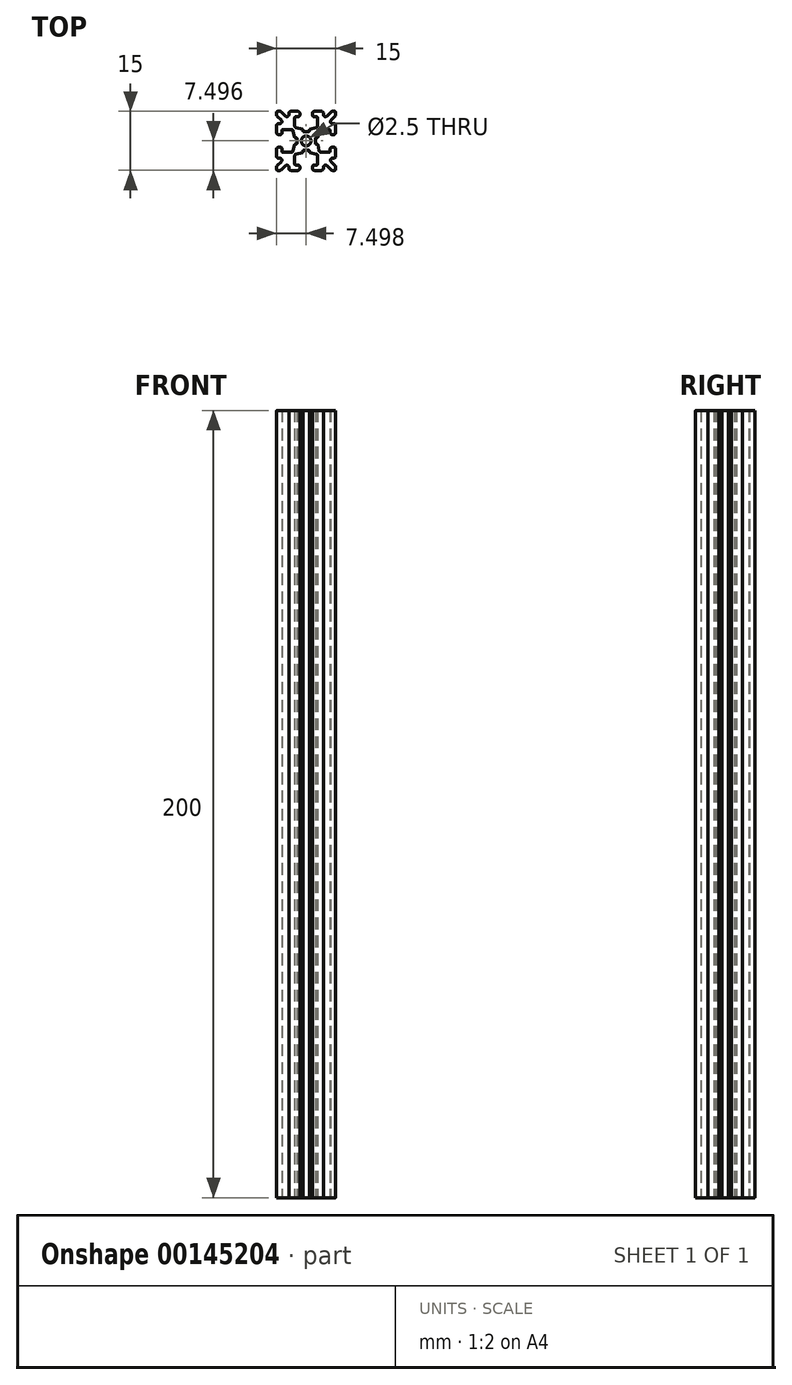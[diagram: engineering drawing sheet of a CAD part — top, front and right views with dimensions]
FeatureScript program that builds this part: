
annotation { "Feature Type Name" : "Feature", "Feature Type Description" : "" }
export const myFeature = defineFeature(function(context is Context, id is Id, definition is map)
    precondition{}
    {
        {
            var Q0;
            Q0=qCreatedBy(makeId("Top.planeOp"),FACE);
            var sketch = newSketch(context, id + "F0", { "sketchPlane" : qUnion([Q0])});
            skCircle(sketch, "E0", {"center": v(-4.16, 17.74) * mm, "radius": 1.25 * mm});
            skArc(sketch, "E1", {"start": v(-3.34, 15.19) * mm, "mid": v(-3.4, 15.33) * mm, "end": v(-3.54, 15.39) * mm});
            skLineSegment(sketch, "E2", {"start": v(-3.54, 15.39) * mm, "end": v(-4.79, 15.39) * mm});
            skArc(sketch, "E3", {"start": v(-4.79, 15.39) * mm, "mid": v(-4.93, 15.33) * mm, "end": v(-4.99, 15.19) * mm});
            skLineSegment(sketch, "E4", {"start": v(-4.99, 15.19) * mm, "end": v(-4.99, 14.96) * mm});
            skArc(sketch, "E5", {"start": v(-5.14, 14.77) * mm, "mid": v(-5.03, 14.84) * mm, "end": v(-4.99, 14.96) * mm});
            skLineSegment(sketch, "E6", {"start": v(-5.14, 14.77) * mm, "end": v(-6.67, 14.42) * mm});
            skArc(sketch, "E7", {"start": v(-6.67, 14.42) * mm, "mid": v(-6.95, 14.25) * mm, "end": v(-7.06, 13.94) * mm});
            skLineSegment(sketch, "E8", {"start": v(-7.06, 13.94) * mm, "end": v(-7.06, 11.84) * mm});
            skArc(sketch, "E9", {"start": v(-7.06, 11.84) * mm, "mid": v(-7, 11.7) * mm, "end": v(-6.86, 11.64) * mm});
            skLineSegment(sketch, "E10", {"start": v(-6.86, 11.64) * mm, "end": v(-6.26, 11.64) * mm});
            skArc(sketch, "E11", {"start": v(-5.76, 11.14) * mm, "mid": v(-5.9, 11.49) * mm, "end": v(-6.26, 11.64) * mm});
            skLineSegment(sketch, "E12", {"start": v(-5.76, 11.14) * mm, "end": v(-5.76, 10.74) * mm});
            skArc(sketch, "E13", {"start": v(-6.26, 10.24) * mm, "mid": v(-5.9, 10.38) * mm, "end": v(-5.76, 10.74) * mm});
            skArc(sketch, "E14", {"start": v(-8.56, 10.74) * mm, "mid": v(-8.42, 10.38) * mm, "end": v(-8.06, 10.24) * mm});
            skLineSegment(sketch, "E15", {"start": v(-8.56, 10.74) * mm, "end": v(-8.56, 11.07) * mm});
            skArc(sketch, "E16", {"start": v(-8.56, 11.07) * mm, "mid": v(-8.87, 11.53) * mm, "end": v(-9.42, 11.42) * mm});
            skLineSegment(sketch, "E17", {"start": v(-9.42, 11.42) * mm, "end": v(-10.45, 10.38) * mm});
            skArc(sketch, "E18", {"start": v(-10.8, 10.24) * mm, "mid": v(-10.62, 10.27) * mm, "end": v(-10.45, 10.38) * mm});
            skArc(sketch, "E19", {"start": v(-11.66, 10.49) * mm, "mid": v(-11.59, 10.3) * mm, "end": v(-11.41, 10.24) * mm});
            skArc(sketch, "E20", {"start": v(-11.52, 11.44) * mm, "mid": v(-11.62, 11.28) * mm, "end": v(-11.66, 11.09) * mm});
            skLineSegment(sketch, "E21", {"start": v(-11.52, 11.44) * mm, "end": v(-10.48, 12.48) * mm});
            skArc(sketch, "E22", {"start": v(-10.48, 12.48) * mm, "mid": v(-10.37, 13.03) * mm, "end": v(-10.83, 13.34) * mm});
            skLineSegment(sketch, "E23", {"start": v(-10.83, 13.34) * mm, "end": v(-11.16, 13.34) * mm});
            skArc(sketch, "E24", {"start": v(-11.66, 13.84) * mm, "mid": v(-11.52, 13.48) * mm, "end": v(-11.16, 13.34) * mm});
            skLineSegment(sketch, "E25", {"start": v(-11.66, 15.64) * mm, "end": v(-11.66, 13.84) * mm});
            skArc(sketch, "E26", {"start": v(-11.16, 16.14) * mm, "mid": v(-11.52, 15.99) * mm, "end": v(-11.66, 15.64) * mm});
            skLineSegment(sketch, "E27", {"start": v(-11.16, 16.14) * mm, "end": v(-10.76, 16.14) * mm});
            skArc(sketch, "E28", {"start": v(-10.26, 15.64) * mm, "mid": v(-10.4, 15.99) * mm, "end": v(-10.76, 16.14) * mm});
            skLineSegment(sketch, "E29", {"start": v(-10.26, 15.64) * mm, "end": v(-10.26, 15.04) * mm});
            skArc(sketch, "E30", {"start": v(-10.26, 15.04) * mm, "mid": v(-10.2, 14.9) * mm, "end": v(-10.06, 14.84) * mm});
            skLineSegment(sketch, "E31", {"start": v(-10.06, 14.84) * mm, "end": v(-7.96, 14.84) * mm});
            skArc(sketch, "E32", {"start": v(-7.96, 14.84) * mm, "mid": v(-7.65, 14.95) * mm, "end": v(-7.47, 15.23) * mm});
            skLineSegment(sketch, "E33", {"start": v(-7.47, 15.23) * mm, "end": v(-7.13, 16.75) * mm});
            skArc(sketch, "E34", {"start": v(-6.94, 16.91) * mm, "mid": v(-7.06, 16.87) * mm, "end": v(-7.13, 16.75) * mm});
            skLineSegment(sketch, "E35", {"start": v(-6.94, 16.91) * mm, "end": v(-6.7, 16.91) * mm});
            skArc(sketch, "E36", {"start": v(-6.7, 16.91) * mm, "mid": v(-6.57, 16.97) * mm, "end": v(-6.5, 17.11) * mm});
            skLineSegment(sketch, "E37", {"start": v(-6.5, 17.11) * mm, "end": v(-6.5, 18.36) * mm});
            skArc(sketch, "E38", {"start": v(-6.5, 18.36) * mm, "mid": v(-6.57, 18.5) * mm, "end": v(-6.7, 18.56) * mm});
            skLineSegment(sketch, "E39", {"start": v(-6.7, 18.56) * mm, "end": v(-6.94, 18.56) * mm});
            skArc(sketch, "E40", {"start": v(-7.13, 18.72) * mm, "mid": v(-7.06, 18.6) * mm, "end": v(-6.94, 18.56) * mm});
            skLineSegment(sketch, "E41", {"start": v(-7.13, 18.72) * mm, "end": v(-7.47, 20.25) * mm});
            skArc(sketch, "E42", {"start": v(-7.47, 20.25) * mm, "mid": v(-7.65, 20.53) * mm, "end": v(-7.96, 20.64) * mm});
            skLineSegment(sketch, "E43", {"start": v(-7.96, 20.64) * mm, "end": v(-10.06, 20.64) * mm});
            skArc(sketch, "E44", {"start": v(-10.06, 20.64) * mm, "mid": v(-10.2, 20.58) * mm, "end": v(-10.26, 20.44) * mm});
            skLineSegment(sketch, "E45", {"start": v(-10.26, 20.44) * mm, "end": v(-10.26, 19.84) * mm});
            skArc(sketch, "E46", {"start": v(-10.76, 19.34) * mm, "mid": v(-10.4, 19.48) * mm, "end": v(-10.26, 19.84) * mm});
            skLineSegment(sketch, "E47", {"start": v(-10.76, 19.34) * mm, "end": v(-11.16, 19.34) * mm});
            skArc(sketch, "E48", {"start": v(-11.66, 19.84) * mm, "mid": v(-11.52, 19.48) * mm, "end": v(-11.16, 19.34) * mm});
            skArc(sketch, "E49", {"start": v(-11.16, 22.14) * mm, "mid": v(-11.52, 21.99) * mm, "end": v(-11.66, 21.64) * mm});
            skLineSegment(sketch, "E50", {"start": v(-11.16, 22.14) * mm, "end": v(-10.83, 22.14) * mm});
            skArc(sketch, "E51", {"start": v(-10.83, 22.14) * mm, "mid": v(-10.37, 22.44) * mm, "end": v(-10.48, 22.99) * mm});
            skLineSegment(sketch, "E52", {"start": v(-10.48, 22.99) * mm, "end": v(-11.52, 24.03) * mm});
            skArc(sketch, "E53", {"start": v(-11.66, 24.38) * mm, "mid": v(-11.62, 24.2) * mm, "end": v(-11.52, 24.03) * mm});
            skArc(sketch, "E54", {"start": v(-11.41, 25.24) * mm, "mid": v(-11.59, 25.16) * mm, "end": v(-11.66, 24.99) * mm});
            skArc(sketch, "E55", {"start": v(-10.45, 25.09) * mm, "mid": v(-10.62, 25.2) * mm, "end": v(-10.8, 25.24) * mm});
            skLineSegment(sketch, "E56", {"start": v(-10.45, 25.09) * mm, "end": v(-9.42, 24.05) * mm});
            skArc(sketch, "E57", {"start": v(-9.42, 24.05) * mm, "mid": v(-8.87, 23.94) * mm, "end": v(-8.56, 24.4) * mm});
            skLineSegment(sketch, "E58", {"start": v(-8.56, 24.4) * mm, "end": v(-8.56, 24.74) * mm});
            skArc(sketch, "E59", {"start": v(-8.06, 25.24) * mm, "mid": v(-8.42, 25.09) * mm, "end": v(-8.56, 24.74) * mm});
            skArc(sketch, "E60", {"start": v(-5.76, 24.74) * mm, "mid": v(-5.9, 25.09) * mm, "end": v(-6.26, 25.24) * mm});
            skLineSegment(sketch, "E61", {"start": v(-5.76, 24.74) * mm, "end": v(-5.76, 24.34) * mm});
            skArc(sketch, "E62", {"start": v(-6.26, 23.84) * mm, "mid": v(-5.9, 23.98) * mm, "end": v(-5.76, 24.34) * mm});
            skLineSegment(sketch, "E63", {"start": v(-6.26, 23.84) * mm, "end": v(-6.86, 23.84) * mm});
            skArc(sketch, "E64", {"start": v(-6.86, 23.84) * mm, "mid": v(-7, 23.78) * mm, "end": v(-7.06, 23.64) * mm});
            skLineSegment(sketch, "E65", {"start": v(-7.06, 23.64) * mm, "end": v(-7.06, 21.54) * mm});
            skArc(sketch, "E66", {"start": v(-7.06, 21.54) * mm, "mid": v(-6.95, 21.22) * mm, "end": v(-6.67, 21.05) * mm});
            skLineSegment(sketch, "E67", {"start": v(-6.67, 21.05) * mm, "end": v(-5.14, 20.7) * mm});
            skArc(sketch, "E68", {"start": v(-4.99, 20.51) * mm, "mid": v(-5.03, 20.64) * mm, "end": v(-5.14, 20.7) * mm});
            skLineSegment(sketch, "E69", {"start": v(-4.99, 20.51) * mm, "end": v(-4.99, 20.28) * mm});
            skArc(sketch, "E70", {"start": v(-4.99, 20.28) * mm, "mid": v(-4.93, 20.14) * mm, "end": v(-4.79, 20.08) * mm});
            skLineSegment(sketch, "E71", {"start": v(-4.79, 20.08) * mm, "end": v(-3.54, 20.08) * mm});
            skArc(sketch, "E72", {"start": v(-3.54, 20.08) * mm, "mid": v(-3.4, 20.14) * mm, "end": v(-3.34, 20.28) * mm});
            skLineSegment(sketch, "E73", {"start": v(-3.34, 20.28) * mm, "end": v(-3.34, 20.51) * mm});
            skArc(sketch, "E74", {"start": v(-3.18, 20.7) * mm, "mid": v(-3.3, 20.64) * mm, "end": v(-3.34, 20.51) * mm});
            skLineSegment(sketch, "E75", {"start": v(-3.18, 20.7) * mm, "end": v(-1.65, 21.05) * mm});
            skArc(sketch, "E76", {"start": v(-1.65, 21.05) * mm, "mid": v(-1.37, 21.22) * mm, "end": v(-1.26, 21.54) * mm});
            skLineSegment(sketch, "E77", {"start": v(-1.26, 21.54) * mm, "end": v(-1.26, 23.64) * mm});
            skArc(sketch, "E78", {"start": v(-1.26, 23.64) * mm, "mid": v(-1.32, 23.78) * mm, "end": v(-1.46, 23.84) * mm});
            skLineSegment(sketch, "E79", {"start": v(-1.46, 23.84) * mm, "end": v(-2.06, 23.84) * mm});
            skArc(sketch, "E80", {"start": v(-2.56, 24.34) * mm, "mid": v(-2.42, 23.98) * mm, "end": v(-2.06, 23.84) * mm});
            skLineSegment(sketch, "E81", {"start": v(-2.56, 24.34) * mm, "end": v(-2.56, 24.74) * mm});
            skArc(sketch, "E82", {"start": v(-2.06, 25.24) * mm, "mid": v(-2.42, 25.09) * mm, "end": v(-2.56, 24.74) * mm});
            skArc(sketch, "E83", {"start": v(0.24, 24.74) * mm, "mid": v(0.1, 25.09) * mm, "end": v(-0.26, 25.24) * mm});
            skLineSegment(sketch, "E84", {"start": v(0.24, 24.74) * mm, "end": v(0.24, 24.4) * mm});
            skArc(sketch, "E85", {"start": v(0.24, 24.4) * mm, "mid": v(0.55, 23.94) * mm, "end": v(1.1, 24.05) * mm});
            skLineSegment(sketch, "E86", {"start": v(1.1, 24.05) * mm, "end": v(2.13, 25.09) * mm});
            skArc(sketch, "E87", {"start": v(2.48, 25.24) * mm, "mid": v(2.3, 25.2) * mm, "end": v(2.13, 25.09) * mm});
            skLineSegment(sketch, "E88", {"start": v(3.09, 25.24) * mm, "end": v(2.48, 25.24) * mm});
            skArc(sketch, "E89", {"start": v(3.34, 24.99) * mm, "mid": v(3.27, 25.16) * mm, "end": v(3.09, 25.24) * mm});
            skArc(sketch, "E90", {"start": v(3.2, 24.03) * mm, "mid": v(3.3, 24.2) * mm, "end": v(3.34, 24.38) * mm});
            skLineSegment(sketch, "E91", {"start": v(3.2, 24.03) * mm, "end": v(2.15, 22.99) * mm});
            skArc(sketch, "E92", {"start": v(2.15, 22.99) * mm, "mid": v(2.04, 22.44) * mm, "end": v(2.5, 22.14) * mm});
            skLineSegment(sketch, "E93", {"start": v(2.5, 22.14) * mm, "end": v(2.84, 22.14) * mm});
            skArc(sketch, "E94", {"start": v(3.34, 21.64) * mm, "mid": v(3.2, 21.99) * mm, "end": v(2.84, 22.14) * mm});
            skArc(sketch, "E95", {"start": v(2.84, 19.34) * mm, "mid": v(3.2, 19.48) * mm, "end": v(3.34, 19.84) * mm});
            skLineSegment(sketch, "E96", {"start": v(2.84, 19.34) * mm, "end": v(2.44, 19.34) * mm});
            skArc(sketch, "E97", {"start": v(1.94, 19.84) * mm, "mid": v(2.08, 19.48) * mm, "end": v(2.44, 19.34) * mm});
            skLineSegment(sketch, "E98", {"start": v(1.94, 19.84) * mm, "end": v(1.94, 20.44) * mm});
            skArc(sketch, "E99", {"start": v(1.94, 20.44) * mm, "mid": v(1.88, 20.58) * mm, "end": v(1.74, 20.64) * mm});
            skLineSegment(sketch, "E100", {"start": v(1.74, 20.64) * mm, "end": v(-0.36, 20.64) * mm});
            skArc(sketch, "E101", {"start": v(-0.36, 20.64) * mm, "mid": v(-0.67, 20.53) * mm, "end": v(-0.85, 20.25) * mm});
            skLineSegment(sketch, "E102", {"start": v(-0.85, 20.25) * mm, "end": v(-1.2, 18.72) * mm});
            skArc(sketch, "E103", {"start": v(-1.39, 18.56) * mm, "mid": v(-1.26, 18.6) * mm, "end": v(-1.2, 18.72) * mm});
            skLineSegment(sketch, "E104", {"start": v(-1.39, 18.56) * mm, "end": v(-1.61, 18.56) * mm});
            skArc(sketch, "E105", {"start": v(-1.61, 18.56) * mm, "mid": v(-1.76, 18.5) * mm, "end": v(-1.81, 18.36) * mm});
            skLineSegment(sketch, "E106", {"start": v(-1.81, 18.36) * mm, "end": v(-1.81, 17.11) * mm});
            skArc(sketch, "E107", {"start": v(-1.81, 17.11) * mm, "mid": v(-1.76, 16.97) * mm, "end": v(-1.61, 16.91) * mm});
            skLineSegment(sketch, "E108", {"start": v(-1.61, 16.91) * mm, "end": v(-1.39, 16.91) * mm});
            skArc(sketch, "E109", {"start": v(-1.2, 16.75) * mm, "mid": v(-1.26, 16.87) * mm, "end": v(-1.39, 16.91) * mm});
            skLineSegment(sketch, "E110", {"start": v(-1.2, 16.75) * mm, "end": v(-0.85, 15.23) * mm});
            skArc(sketch, "E111", {"start": v(-0.85, 15.23) * mm, "mid": v(-0.67, 14.95) * mm, "end": v(-0.36, 14.84) * mm});
            skLineSegment(sketch, "E112", {"start": v(-0.36, 14.84) * mm, "end": v(1.74, 14.84) * mm});
            skArc(sketch, "E113", {"start": v(1.74, 14.84) * mm, "mid": v(1.88, 14.9) * mm, "end": v(1.94, 15.04) * mm});
            skLineSegment(sketch, "E114", {"start": v(1.94, 15.04) * mm, "end": v(1.94, 15.64) * mm});
            skArc(sketch, "E115", {"start": v(2.44, 16.14) * mm, "mid": v(2.08, 15.99) * mm, "end": v(1.94, 15.64) * mm});
            skLineSegment(sketch, "E116", {"start": v(2.44, 16.14) * mm, "end": v(2.84, 16.14) * mm});
            skArc(sketch, "E117", {"start": v(3.34, 15.64) * mm, "mid": v(3.2, 15.99) * mm, "end": v(2.84, 16.14) * mm});
            skLineSegment(sketch, "E118", {"start": v(3.34, 13.84) * mm, "end": v(3.34, 15.64) * mm});
            skArc(sketch, "E119", {"start": v(2.84, 13.34) * mm, "mid": v(3.2, 13.48) * mm, "end": v(3.34, 13.84) * mm});
            skLineSegment(sketch, "E120", {"start": v(2.84, 13.34) * mm, "end": v(2.5, 13.34) * mm});
            skArc(sketch, "E121", {"start": v(2.5, 13.34) * mm, "mid": v(2.04, 13.03) * mm, "end": v(2.15, 12.48) * mm});
            skLineSegment(sketch, "E122", {"start": v(2.15, 12.48) * mm, "end": v(3.2, 11.44) * mm});
            skArc(sketch, "E123", {"start": v(3.34, 11.09) * mm, "mid": v(3.3, 11.28) * mm, "end": v(3.2, 11.44) * mm});
            skArc(sketch, "E124", {"start": v(3.09, 10.24) * mm, "mid": v(3.27, 10.3) * mm, "end": v(3.34, 10.49) * mm});
            skLineSegment(sketch, "E125", {"start": v(2.48, 10.24) * mm, "end": v(3.09, 10.24) * mm});
            skArc(sketch, "E126", {"start": v(2.13, 10.38) * mm, "mid": v(2.3, 10.27) * mm, "end": v(2.48, 10.24) * mm});
            skLineSegment(sketch, "E127", {"start": v(2.13, 10.38) * mm, "end": v(1.1, 11.42) * mm});
            skArc(sketch, "E128", {"start": v(1.1, 11.42) * mm, "mid": v(0.55, 11.53) * mm, "end": v(0.24, 11.07) * mm});
            skLineSegment(sketch, "E129", {"start": v(0.24, 11.07) * mm, "end": v(0.24, 10.74) * mm});
            skArc(sketch, "E130", {"start": v(-0.26, 10.24) * mm, "mid": v(0.1, 10.38) * mm, "end": v(0.24, 10.74) * mm});
            skArc(sketch, "E131", {"start": v(-2.56, 10.74) * mm, "mid": v(-2.42, 10.38) * mm, "end": v(-2.06, 10.24) * mm});
            skLineSegment(sketch, "E132", {"start": v(-2.56, 10.74) * mm, "end": v(-2.56, 11.14) * mm});
            skArc(sketch, "E133", {"start": v(-2.06, 11.64) * mm, "mid": v(-2.42, 11.49) * mm, "end": v(-2.56, 11.14) * mm});
            skLineSegment(sketch, "E134", {"start": v(-2.06, 11.64) * mm, "end": v(-1.46, 11.64) * mm});
            skArc(sketch, "E135", {"start": v(-1.46, 11.64) * mm, "mid": v(-1.32, 11.7) * mm, "end": v(-1.26, 11.84) * mm});
            skLineSegment(sketch, "E136", {"start": v(-1.26, 11.84) * mm, "end": v(-1.26, 13.94) * mm});
            skArc(sketch, "E137", {"start": v(-1.26, 13.94) * mm, "mid": v(-1.37, 14.25) * mm, "end": v(-1.65, 14.42) * mm});
            skLineSegment(sketch, "E138", {"start": v(-1.65, 14.42) * mm, "end": v(-3.18, 14.77) * mm});
            skArc(sketch, "E139", {"start": v(-3.34, 14.96) * mm, "mid": v(-3.3, 14.84) * mm, "end": v(-3.18, 14.77) * mm});
            skLineSegment(sketch, "E140", {"start": v(-3.34, 14.96) * mm, "end": v(-3.34, 15.19) * mm});
            skLineSegment(sketch, "E141", {"start": v(-11.66, 21.64) * mm, "end": v(-11.66, 19.84) * mm});
            skLineSegment(sketch, "E142", {"start": v(-10.8, 25.24) * mm, "end": v(-11.41, 25.24) * mm});
            skLineSegment(sketch, "E143", {"start": v(-8.06, 10.24) * mm, "end": v(-6.26, 10.24) * mm});
            skLineSegment(sketch, "E144", {"start": v(3.34, 19.84) * mm, "end": v(3.34, 21.64) * mm});
            skLineSegment(sketch, "E145", {"start": v(-11.66, 24.99) * mm, "end": v(-11.66, 24.38) * mm});
            skLineSegment(sketch, "E146", {"start": v(3.34, 10.49) * mm, "end": v(3.34, 11.09) * mm});
            skLineSegment(sketch, "E147", {"start": v(3.34, 24.38) * mm, "end": v(3.34, 24.99) * mm});
            skLineSegment(sketch, "E148", {"start": v(-6.26, 25.24) * mm, "end": v(-8.06, 25.24) * mm});
            skLineSegment(sketch, "E149", {"start": v(-11.66, 11.09) * mm, "end": v(-11.66, 10.49) * mm});
            skLineSegment(sketch, "E150", {"start": v(-0.26, 25.24) * mm, "end": v(-2.06, 25.24) * mm});
            skLineSegment(sketch, "E151", {"start": v(-2.06, 10.24) * mm, "end": v(-0.26, 10.24) * mm});
            skLineSegment(sketch, "E152", {"start": v(-11.41, 10.24) * mm, "end": v(-10.8, 10.24) * mm});
            skLineSegment(sketch, "E153", {"start": v(-4.16, 17.74) * mm, "end": v(-4.16, 20.24) * mm});
            skLineSegment(sketch, "E154", {"start": v(-4.16, 17.74) * mm, "end": v(-6.66, 17.74) * mm});
            skLineSegment(sketch, "E155", {"start": v(-4.16, 17.74) * mm, "end": v(-4.16, 15.24) * mm});
            skLineSegment(sketch, "E156", {"start": v(-4.16, 17.74) * mm, "end": v(-1.66, 17.74) * mm});
            skLineSegment(sketch, "E157", {"start": v(-4.16, 20.24) * mm, "end": v(-4.16, 21.49) * mm});
            skLineSegment(sketch, "E158", {"start": v(-6.66, 17.74) * mm, "end": v(-7.91, 17.74) * mm});
            skLineSegment(sketch, "E159", {"start": v(-4.16, 15.24) * mm, "end": v(-4.16, 13.99) * mm});
            skLineSegment(sketch, "E160", {"start": v(-1.66, 17.74) * mm, "end": v(-0.41, 17.74) * mm});
            skSolve(sketch);
        }
        {
            var Q0;
            Q0 = qSketchRegion(id + "F0", true);
            var Q1;
            {var subQ5=sQuery(id+"F0.wireOp",EDGE,"E3");Q1=makeQuery(id+"F0.imprint","IMPRINT",FACE,{"disambiguationData":[TD([[makeQuery(id+"F0.imprint","IMPRINT",EDGE,{"derivedFrom":subQ5}),-1.0]])]});}
            var Q2;
            {var subQ0=sQuery(id+"F0.wireOp",EDGE,"E38");Q2=makeQuery(id+"F0.imprint","IMPRINT",FACE,{"disambiguationData":[TD([[makeQuery(id+"F0.imprint","IMPRINT",EDGE,{"derivedFrom":subQ0}),-1.0]])]});}
            var Q3;
            {var subQ7=sQuery(id+"F0.wireOp",EDGE,"E72");Q3=makeQuery(id+"F0.imprint","IMPRINT",FACE,{"disambiguationData":[TD([[makeQuery(id+"F0.imprint","IMPRINT",EDGE,{"derivedFrom":subQ7}),-1.0]])]});}
            extrude(context, id + "F1", {"entities" : qUnion([Q0, Q1, Q2, Q3]), "depth" : 200 * mm});
        }
    });
